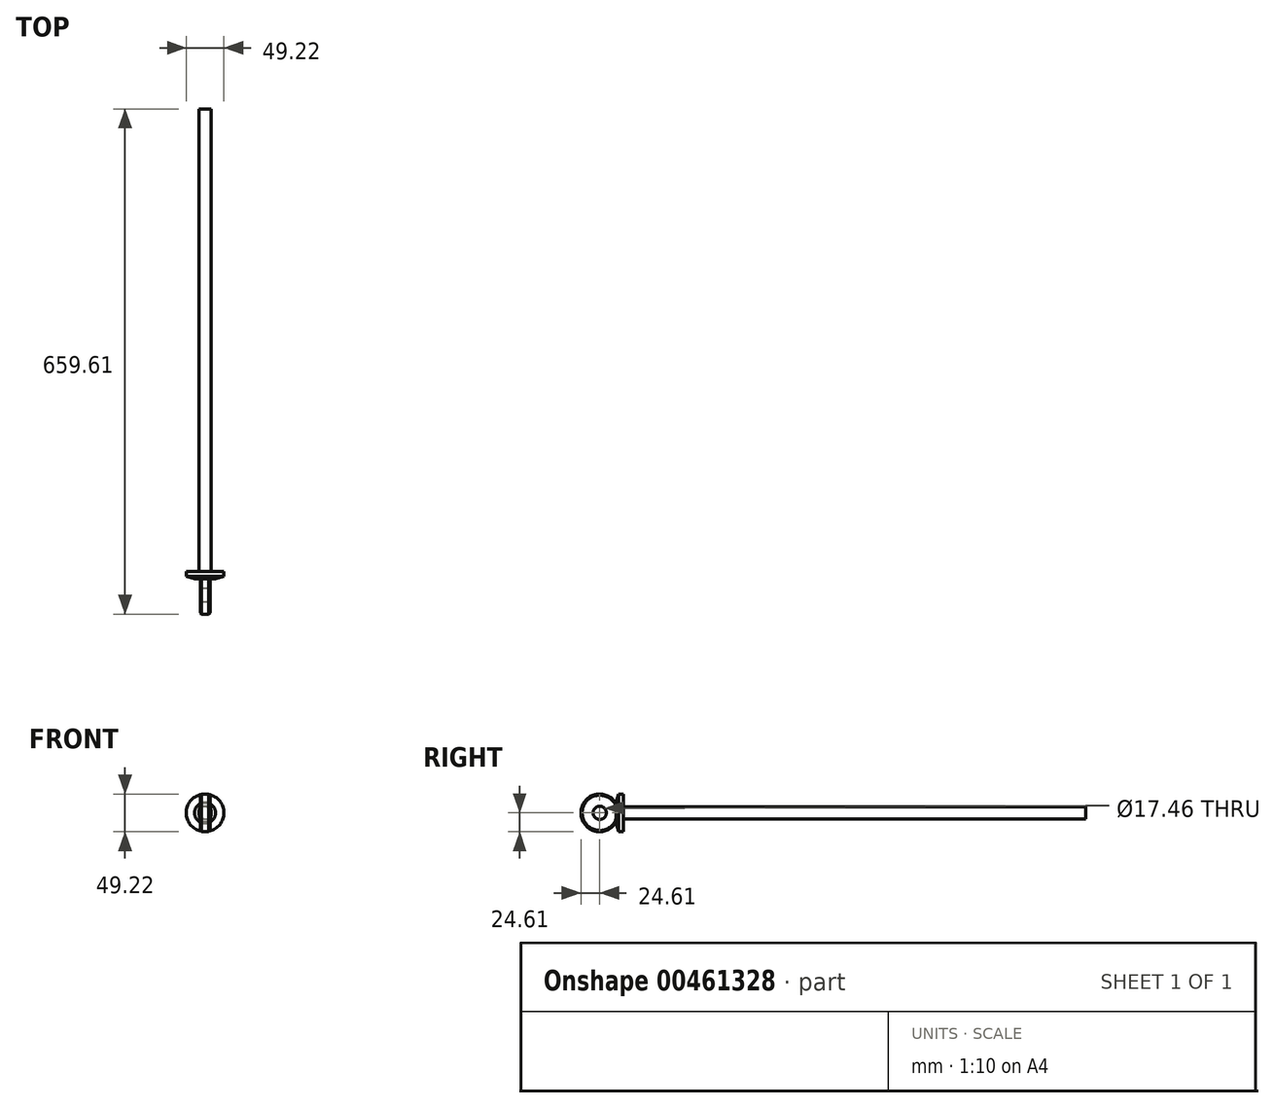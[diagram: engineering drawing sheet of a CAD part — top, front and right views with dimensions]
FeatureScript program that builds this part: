
annotation { "Feature Type Name" : "Feature", "Feature Type Description" : "" }
export const myFeature = defineFeature(function(context is Context, id is Id, definition is map)
    precondition{}
    {
        {
            var Q0;
            Q0=qCreatedBy(makeId("Right.planeOp"),FACE);
            var sketch = newSketch(context, id + "F0", { "sketchPlane" : qUnion([Q0])});
            skCircle(sketch, "E0", {"center": v(0, 0) * mm, "radius": 8.73 * mm});
            skCircle(sketch, "E1", {"center": v(0, 0) * mm, "radius": 24.6 * mm});
            skSolve(sketch);
        }
        {
            var Q0;
            Q0=makeQuery(id+"F0.imprint","IMPRINT",FACE,{"disambiguationData":[TD([[makeQuery(id+"F0.imprint","IMPRINT",EDGE,{"derivedFrom":sQuery(id+"F0.wireOp",EDGE,"E0")}),-1.0]])]});
            extrude(context, id + "F1", {"entities" : qUnion([Q0]), "endBound" : BoundingType.SYMMETRIC, "depth" : 12.7 * mm});
        }
        {
            var Q0;
            Q0=qCreatedBy(makeId("Front.planeOp"),FACE);
            var sketch = newSketch(context, id + "F2", { "sketchPlane" : qUnion([Q0])});
            skCircle(sketch, "E2", {"center": v(0, 0) * mm, "radius": 7.94 * mm});
            skSolve(sketch);
        }
        {
            var Q0;
            Q0 = qSketchRegion(id + "F2", true);
            extrude(context, id + "F3", {"entities" : qUnion([Q0]), "operationType" : NewBodyOperationType.ADD, "oppositeDirection" : true, "depth" : 635 * mm});
        }
        {
            var Q0;
            Q0=qCreatedBy(makeId("Right.planeOp"),FACE);
            var sketch = newSketch(context, id + "F4", { "sketchPlane" : qUnion([Q0])});
            skCircle(sketch, "E3", {"center": v(0, 0) * mm, "radius": 8.73 * mm});
            skSolve(sketch);
        }
        {
            var Q0;
            Q0=makeQuery(id+"F4.imprint","IMPRINT",FACE,{"disambiguationData":[TD([[makeQuery(id+"F4.imprint","IMPRINT",EDGE,{"derivedFrom":sQuery(id+"F4.wireOp",EDGE,"E3")}),1.0]])]});
            extrude(context, id + "F5", {"entities" : qUnion([Q0]), "operationType" : NewBodyOperationType.REMOVE, "endBound" : BoundingType.SYMMETRIC, "oppositeDirection" : true, "depth" : 25.4 * mm});
        }
        {
            var Q0;
            Q0=makeQuery(id+"F1.opExtrude","CAP_FACE",FACE,{"disambiguationData":[OSD([sQuery(id+"F0.wireOp",EDGE,"E0"),sQuery(id+"F0.wireOp",EDGE,"E1")])],"isStart":false});
            var sketch = newSketch(context, id + "F6", { "sketchPlane" : qUnion([Q0])});
            skCircle(sketch, "E4", {"center": v(0, 0) * mm, "radius": 24.6 * mm});
            skSolve(sketch);
        }
        {
            var Q0;
            Q0 = qSketchRegion(id + "F6", true);
            extrude(context, id + "F7", {"entities" : qUnion([Q0]), "operationType" : NewBodyOperationType.REMOVE, "depth" : 25.4 * mm});
        }
        {
            var Q0;
            Q0=makeQuery(id+"F1.opExtrude","CAP_FACE",FACE,{"disambiguationData":[OSD([sQuery(id+"F0.wireOp",EDGE,"E0"),sQuery(id+"F0.wireOp",EDGE,"E1")])],"isStart":true});
            var sketch = newSketch(context, id + "F8", { "sketchPlane" : qUnion([Q0])});
            skCircle(sketch, "E5", {"center": v(0, 0) * mm, "radius": 24.6 * mm});
            skSolve(sketch);
        }
        {
            var Q0;
            Q0 = qSketchRegion(id + "F8", true);
            extrude(context, id + "F9", {"entities" : qUnion([Q0]), "operationType" : NewBodyOperationType.REMOVE, "depth" : 25.4 * mm});
        }
        {
            var Q0;
            Q0=makeQuery(id+"F9.boolean.opBoolean","INTERSECT",EDGE,{"derivedFrom":[makeQuery(id+"F3.opExtrude","SWEPT_FACE",FACE,{"disambiguationData":[OSD([sQuery(id+"F2.wireOp",EDGE,"E2")])]}),makeQuery(id+"F9.opExtrude","SWEPT_FACE",FACE,{"disambiguationData":[OSD([sQuery(id+"F8.wireOp",EDGE,"E5")])]})]});
            cPoint(context, id + "F10", {"entities" : qUnion([Q0]), "parameter" : 0.5});
        }
        {
            var Q0;
            Q0=qCreatedBy(makeId("Front.planeOp"),FACE);
            var Q1;
            Q1 = qCreatedBy(id + "F10" ,VERTEX);
            cPlane(context, id + "F11", {"entities" : qUnion([Q0, Q1]), "cplaneType" : CPlaneType.PLANE_POINT, "offset" : 25.4 * mm, "width" : 152.4 * mm, "height" : 152.4 * mm});
        }
        {
            var Q0;
            Q0=qCreatedBy(id+"F11.planeOp",FACE);
            var sketch = newSketch(context, id + "F12", { "sketchPlane" : qUnion([Q0])});
            skCircle(sketch, "E6", {"center": v(0, 0) * mm, "radius": 24.6 * mm});
            skSolve(sketch);
        }
        {
            var Q0;
            Q0=makeQuery(id+"F12.imprint","IMPRINT",FACE,{"disambiguationData":[TD([[makeQuery(id+"F12.imprint","IMPRINT",EDGE,{"derivedFrom":sQuery(id+"F12.wireOp",EDGE,"E6")}),1.0]])]});
            extrude(context, id + "F13", {"entities" : qUnion([Q0]), "operationType" : NewBodyOperationType.ADD, "oppositeDirection" : true, "depth" : 6.35 * mm, "hasSecondDirection" : true, "secondDirectionOppositeDirection" : false, "secondDirectionDepth" : 3.17 * mm, "hasSecondDirectionDraft" : true, "secondDirectionDraftAngle" : 73.75 * degree, "secondDirectionDraftPullDirection" : true});
        }
        {
            var Q0;
            Q0=makeQuery(id+"F1.opExtrude","CAP_EDGE",EDGE,{"disambiguationData":[OSD([sQuery(id+"F0.wireOp",EDGE,"E1")])],"isStart":true});
            var Q1;
            Q1=makeQuery(id+"F1.opExtrude","CAP_EDGE",EDGE,{"disambiguationData":[OSD([sQuery(id+"F0.wireOp",EDGE,"E1")])],"isStart":false});
            chamfer(context, id + "F14", {"entities" : qUnion([Q0, Q1]), "width" : 1.59 * mm, "tangentPropagation" : true});
        }
        {
            var Q0;
            Q0=makeQuery(id+"F13.boolean.opBoolean","INTERSECT",EDGE,{"derivedFrom":[makeQuery(id+"F9.boolean.opBoolean","MERGE",FACE,{"derivedFrom":[makeQuery(id+"F1.opExtrude","CAP_FACE",FACE,{"disambiguationData":[OSD([sQuery(id+"F0.wireOp",EDGE,"E0"),sQuery(id+"F0.wireOp",EDGE,"E1")])],"isStart":true}),makeQuery(id+"F9.opExtrude","CAP_FACE",FACE,{"disambiguationData":[OSD([sQuery(id+"F8.wireOp",EDGE,"E5")])],"isStart":true})]}),makeQuery(id+"F13.opExtrude","CAP_FACE",FACE,{"disambiguationData":[OSD([sQuery(id+"F12.wireOp",EDGE,"E6")])],"isStart":true})]});
            var Q1;
            Q1=makeQuery(id+"F13.boolean.opBoolean","INTERSECT",EDGE,{"derivedFrom":[makeQuery(id+"F7.boolean.opBoolean","MERGE",FACE,{"derivedFrom":[makeQuery(id+"F1.opExtrude","CAP_FACE",FACE,{"disambiguationData":[OSD([sQuery(id+"F0.wireOp",EDGE,"E0"),sQuery(id+"F0.wireOp",EDGE,"E1")])],"isStart":false}),makeQuery(id+"F7.opExtrude","CAP_FACE",FACE,{"disambiguationData":[OSD([sQuery(id+"F6.wireOp",EDGE,"E4")])],"isStart":true})]}),makeQuery(id+"F13.opExtrude","CAP_FACE",FACE,{"disambiguationData":[OSD([sQuery(id+"F12.wireOp",EDGE,"E6")])],"isStart":true})]});
            fillet(context, id + "F15", {"entities" : qUnion([Q0, Q1]), "radius" : 1.59 * mm, "tangentPropagation" : true, "rho" : 0.5, "crossSection" : FilletCrossSection.CONIC, "allowEdgeOverflow" : false});
        }
    });
